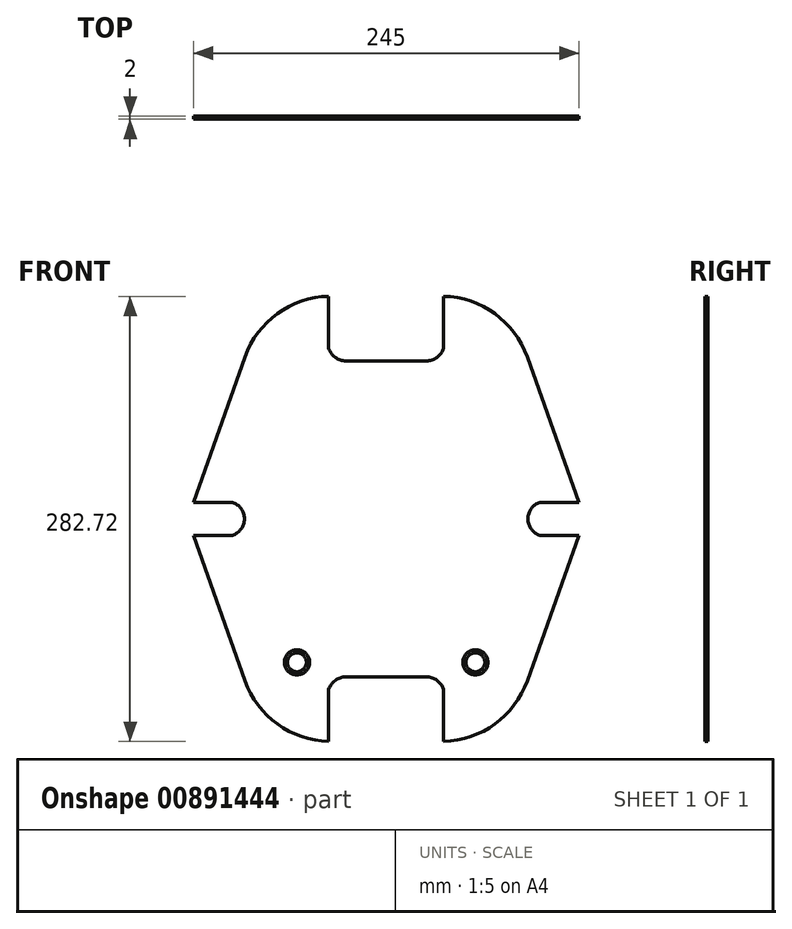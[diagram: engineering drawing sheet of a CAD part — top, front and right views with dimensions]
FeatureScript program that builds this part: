
annotation { "Feature Type Name" : "Feature", "Feature Type Description" : "" }
export const myFeature = defineFeature(function(context is Context, id is Id, definition is map)
    precondition{}
    {
        {
            var Q0;
            Q0=qCreatedBy(makeId("Front.planeOp"),FACE);
            var sketch = newSketch(context, id + "F0", { "sketchPlane" : qUnion([Q0])});
            skLineSegment(sketch, "E0", {"start": v(-122.5, 130.86) * mm, "end": v(122.5, 130.86) * mm});
            skLineSegment(sketch, "E1", {"start": v(122.5, 130.86) * mm, "end": v(89.64, 38.53) * mm});
            skLineSegment(sketch, "E2", {"start": v(-122.5, 130.86) * mm, "end": v(-89.64, 38.53) * mm});
            skArc(sketch, "E3", {"start": v(-89.64, 38.53) * mm, "mid": v(-69.05, 11.03) * mm, "end": v(-36.5, 0) * mm});
            skArc(sketch, "E4", {"start": v(36.5, 0) * mm, "mid": v(69.05, 11.03) * mm, "end": v(89.64, 38.53) * mm});
            skLineSegment(sketch, "E5", {"start": v(-36.5, 0) * mm, "end": v(-36.5, 33) * mm});
            skLineSegment(sketch, "E6", {"start": v(-36.5, 33) * mm, "end": v(36.5, 33) * mm, "construction": true});
            skLineSegment(sketch, "E7", {"start": v(36.5, 33) * mm, "end": v(36.5, 0) * mm});
            skLineSegment(sketch, "E8", {"start": v(0, 33) * mm, "end": v(0, 0) * mm, "construction": true});
            skLineSegment(sketch, "E9", {"start": v(-25.5, 41) * mm, "end": v(25.5, 41) * mm});
            skArc(sketch, "E10", {"start": v(-25.5, 41) * mm, "mid": v(-32.3, 38.79) * mm, "end": v(-36.5, 33) * mm});
            skArc(sketch, "E11", {"start": v(36.5, 33) * mm, "mid": v(32.3, 38.79) * mm, "end": v(25.5, 41) * mm});
            skPoint(sketch, "E12", {"position": v(-56.67, 50.27) * mm});
            skPoint(sketch, "E13", {"position": v(56.67, 50.27) * mm});
            skLineSegment(sketch, "E14", {"start": v(-89.64, 38.53) * mm, "end": v(-56.67, 50.27) * mm, "construction": true});
            skSolve(sketch);
        }
        {
            var Q0;
            Q0 = qSketchRegion(id + "F0", true);
            extrude(context, id + "F1", {"entities" : qUnion([Q0]), "oppositeDirection" : true, "depth" : 2 * mm, "offsetDistance" : 25 * mm});
        }
        {
            var Q0;
            Q0=makeQuery(id+"F1.opExtrude","SWEPT_FACE",FACE,{"disambiguationData":[OSD([sQuery(id+"F0.wireOp",EDGE,"E0")])]});
            cPlane(context, id + "F2", {"entities" : qUnion([Q0]), "cplaneType" : CPlaneType.OFFSET, "offset" : 10.5 * mm, "width" : 150 * mm, "height" : 150 * mm});
        }
        {
            var Q0;
            Q0=makeQuery(id+"F1.opExtrude","SWEPT_BODY",BODY,{"disambiguationData":[OSD([sQuery(id+"F0.wireOp",EDGE,"E0"),sQuery(id+"F0.wireOp",EDGE,"E1"),sQuery(id+"F0.wireOp",EDGE,"E2"),sQuery(id+"F0.wireOp",EDGE,"E3"),sQuery(id+"F0.wireOp",EDGE,"RBLw4Hvx-HNYR-cSoG-CBft-1KmUEeb84xH9"),sQuery(id+"F0.wireOp",EDGE,"E4")])]});
            var Q1;
            Q1=qCreatedBy(id+"F2.planeOp",FACE);
            mirror(context, id + "F3", {"entities" : qUnion([Q0]), "mirrorPlane" : qUnion([Q1])});
        }
        {
            var Q0;
            Q0=makeQuery(id+"F1.opExtrude","CAP_FACE",FACE,{"disambiguationData":[OSD([sQuery(id+"F0.wireOp",EDGE,"E0"),sQuery(id+"F0.wireOp",EDGE,"E1"),sQuery(id+"F0.wireOp",EDGE,"E2"),sQuery(id+"F0.wireOp",EDGE,"E3"),sQuery(id+"F0.wireOp",EDGE,"RBLw4Hvx-HNYR-cSoG-CBft-1KmUEeb84xH9"),sQuery(id+"F0.wireOp",EDGE,"E4")])],"isStart":true});
            var sketch = newSketch(context, id + "F4", { "sketchPlane" : qUnion([Q0])});
            skArc(sketch, "E15", {"start": v(-97.72, 130.86) * mm, "mid": v(-90, 141.36) * mm, "end": v(-97.72, 151.86) * mm});
            skArc(sketch, "E16", {"start": v(97.72, 151.86) * mm, "mid": v(90, 141.36) * mm, "end": v(97.72, 130.86) * mm});
            skLineSegment(sketch, "E17", {"start": v(-90, 141.36) * mm, "end": v(90, 141.36) * mm, "construction": true});
            skLineSegment(sketch, "E18", {"start": v(0, 130.86) * mm, "end": v(0, 141.36) * mm, "construction": true});
            skLineSegment(sketch, "E19", {"start": v(-97.72, 151.86) * mm, "end": v(97.72, 151.86) * mm});
            skLineSegment(sketch, "E20", {"start": v(-97.72, 130.86) * mm, "end": v(97.72, 130.86) * mm});
            skSolve(sketch);
        }
        {
            var Q0;
            Q0 = qSketchRegion(id + "F4", true);
            extrude(context, id + "F5", {"entities" : qUnion([Q0]), "operationType" : NewBodyOperationType.ADD, "oppositeDirection" : true, "depth" : 2 * mm, "offsetDistance" : 25 * mm});
        }
        {
            var Q0;
            Q0=sQuery(id+"F0.wireOp",VERTEX,"E12");
            var Q1;
            Q1=sQuery(id+"F0.wireOp",VERTEX,"E13");
            var Q2;
            Q2=makeQuery(id+"F1.opExtrude","SWEPT_BODY",BODY,{"disambiguationData":[OSD([sQuery(id+"F0.wireOp",EDGE,"E0"),sQuery(id+"F0.wireOp",EDGE,"E1"),sQuery(id+"F0.wireOp",EDGE,"E2"),sQuery(id+"F0.wireOp",EDGE,"E3"),sQuery(id+"F0.wireOp",EDGE,"E4"),sQuery(id+"F0.wireOp",EDGE,"E5"),sQuery(id+"F0.wireOp",EDGE,"E7"),sQuery(id+"F0.wireOp",EDGE,"E9"),sQuery(id+"F0.wireOp",EDGE,"E10"),sQuery(id+"F0.wireOp",EDGE,"E11")])]});
            hole(context, id + "F6", {"style" : HoleStyle.C_SINK, "endStyle" : HoleEndStyle.THROUGH, "holeDiameter" : 8 * mm, "cSinkDiameter" : 16 * mm, "cSinkAngle" : 90 * degree, "majorDiameter" : 5 * mm, "isTappedThrough" : true, "tappedDepth" : 12 * mm, "tapClearance" : 3, "locations" : qUnion([Q0, Q1]), "scope" : qUnion([Q2])});
        }
    });
